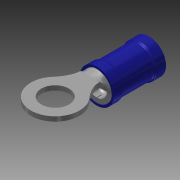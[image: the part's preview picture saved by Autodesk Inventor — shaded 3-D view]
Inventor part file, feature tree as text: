
AUTODESK INVENTOR PART (.ipt)
format: ipt  version: 2014 (Build 180170000, 170)  size: 440,320 bytes
history: native  units: in
note: dims shown in document units (in); Inventor stores cm internally (conversion verified against a paired STEP export)
features: sketch x6, fillet x5, projected_geometry x5, extrude x4, mirror x1, shell x1, revolve x1, plane x1, loft x1, chamfer x1, other x1
ambient origin geometry x8: Origin, YZ Plane, XZ Plane, XY Plane, X Axis, Y Axis, Z Axis, Center Point
bodies: Solid1 (feature_tree), Solid2 (feature_tree)
feature tree (27):
  extrude  "Extrusion1"  Depth=0.229in TaperAngle=0.0deg
  extrude  "Extrusion2"  Depth=0.068in TaperAngle=0.0deg
  fillet  "Fillet1"  Radius=0.01in
  mirror  "Mirror1"
  shell  "Shell1"  Thickness=0.0175in
  revolve  "Revolution1"  [1 undecoded]
  plane  "Work Plane1"
  extrude  "Extrusion3"  Depth=0.082in
  loft  "Loft1"
  fillet  "Fillet2"  Radius=0.339in
  fillet  "Fillet3"  Radius=0.073in
  fillet  "Fillet4"  Radius=0.032in
  fillet  "Fillet5"  [1 undecoded]
  chamfer  "Chamfer1"  Angle=90.0deg  [1 undecoded]
  extrude  "Extrusion4"  Depth=0.032in
  sketch  "Sketch1"  dims[d0=0.219in d1=0.229in d2=0.0in]
  sketch  "Sketch2"  dims[d3=0.236in d4=0.068in d5=0.0in d6=0.01in d7=0.0175in]
  projected_geometry  "Projected Loop1"
  sketch  "Sketch3"  dims[d8=0.031in d9=0.031in]
  sketch  "Sketch4"  dims[d10=90.0deg d11=0.082in]
  projected_geometry  "Projected Loop2"
  sketch  "Sketch5"  dims[d12=0.2905in d13=0.0495in d14=0.339in d15=0.073in d16=0.032in d17=0.0in d18=0.0in d19=90.0deg d20=0.0in d21=90.0deg]
  projected_geometry  "Projected Loop3"
  other  "Edges1"
  sketch  "Sketch6"  dims[d22=0.1in d23=0.015in d24=0.02in d25=0.02in d26=0.003in d27=0.125in d28=45.0deg d29=0.005in d30=0.032in d31=0.0in]
  projected_geometry  "Project Cut Edges1"
  projected_geometry  "Project Cut Edges2"
note: 3 required parameter values undecoded (feature->parameter linkage not recoverable at this tier; creation-order binding heuristic only, values carry confidence <= 0.55)